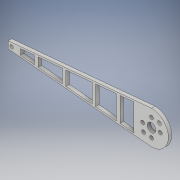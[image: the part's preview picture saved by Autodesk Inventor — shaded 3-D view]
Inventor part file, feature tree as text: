
AUTODESK INVENTOR PART (.ipt)
format: ipt  version: 2017 (Build 210142000, 142)  size: 244,224 bytes
history: native  units: in
note: dims shown in document units (in); Inventor stores cm internally (conversion verified against a paired STEP export)
features: extrude x15, sketch x11, plane x1, projected_geometry x1
ambient origin geometry x8: Origin, YZ Plane, XZ Plane, XY Plane, X Axis, Y Axis, Z Axis, Center Point
bodies: Solid1 (feature_tree)
feature tree (28):
  sketch  "Sketch1"  dims[d0=1.2in d1=0.125in d2=0.0in]
  extrude  "Extrusion1"  Depth=0.125in TaperAngle=0.0deg
  sketch  "Sketch2"  dims[d3=0.125in d4=0.125in]
  plane  "Work Plane1"
  extrude  "Extrusion2"  Depth=0.125in
  extrude  "Extrusion3"  Depth=4.5295in TaperAngle=0.0deg
  extrude  "Extrusion4"  Depth=0.315in
  extrude  "Extrusion5"  Depth=0.315in
  extrude  "Extrusion7"  Depth=0.315in
  extrude  "Extrusion9"  Depth=0.138in
  sketch  "Sketch11"  dims[d18=0.138in d19=0.5in d20=0.0in]
  extrude  "Extrusion11"  Depth=0.5in TaperAngle=0.0deg
  extrude  "Extrusion12"  Depth=0.5in TaperAngle=0.0deg
  sketch  "Sketch12"  dims[d21=0.314in d22=0.5in d23=0.0in]
  extrude  "Extrusion13"  Depth=0.125in
  extrude  "Extrusion14"  Depth=0.125in
  extrude  "Extrusion15"  TaperAngle=45.0deg  [1 undecoded]
  sketch  "Sketch19"  dims[d28=0.125in d29=0.0in d37=0.4in d38=45.0deg d39=0.4in d40=0.138in d41=0.138in d42=1.0in d43=0.0in d47=1.0in d48=1.0in d49=0.0in d50=1.0in d51=1.0in d52=0.0in d53=0.125in d54=0.0in d55=0.125in d56=0.0in d63=0.125in d64=0.0in d71=0.125in d72=0.125in d73=0.125in d74=0.0in d77=0.125in d78=0.0in d80=0.125in d81=0.125in d82=0.0in]
  extrude  "Extrusion16"  Depth=0.125in
  extrude  "Extrusion17"  Depth=0.125in
  extrude  "Extrusion18"  Depth=0.125in
  sketch  "Sketch3"  dims[d6=0.25in d7=4.5295in d8=0.0in]
  sketch  "Sketch4"  dims[d9=0.5in d10=0.0in d11=0.315in]
  sketch  "Sketch5"  dims[d12=0.315in d13=0.315in]
  sketch  "Sketch7"  dims[d14=0.315in d15=0.138in]
  sketch  "Sketch9"  dims[d16=0.138in d17=0.138in]
  sketch  "Sketch16"  dims[d26=0.125in d27=0.125in]
  projected_geometry  "Projected Loop1"
note: 1 required parameter value undecoded (feature->parameter linkage not recoverable at this tier; creation-order binding heuristic only, values carry confidence <= 0.55)
